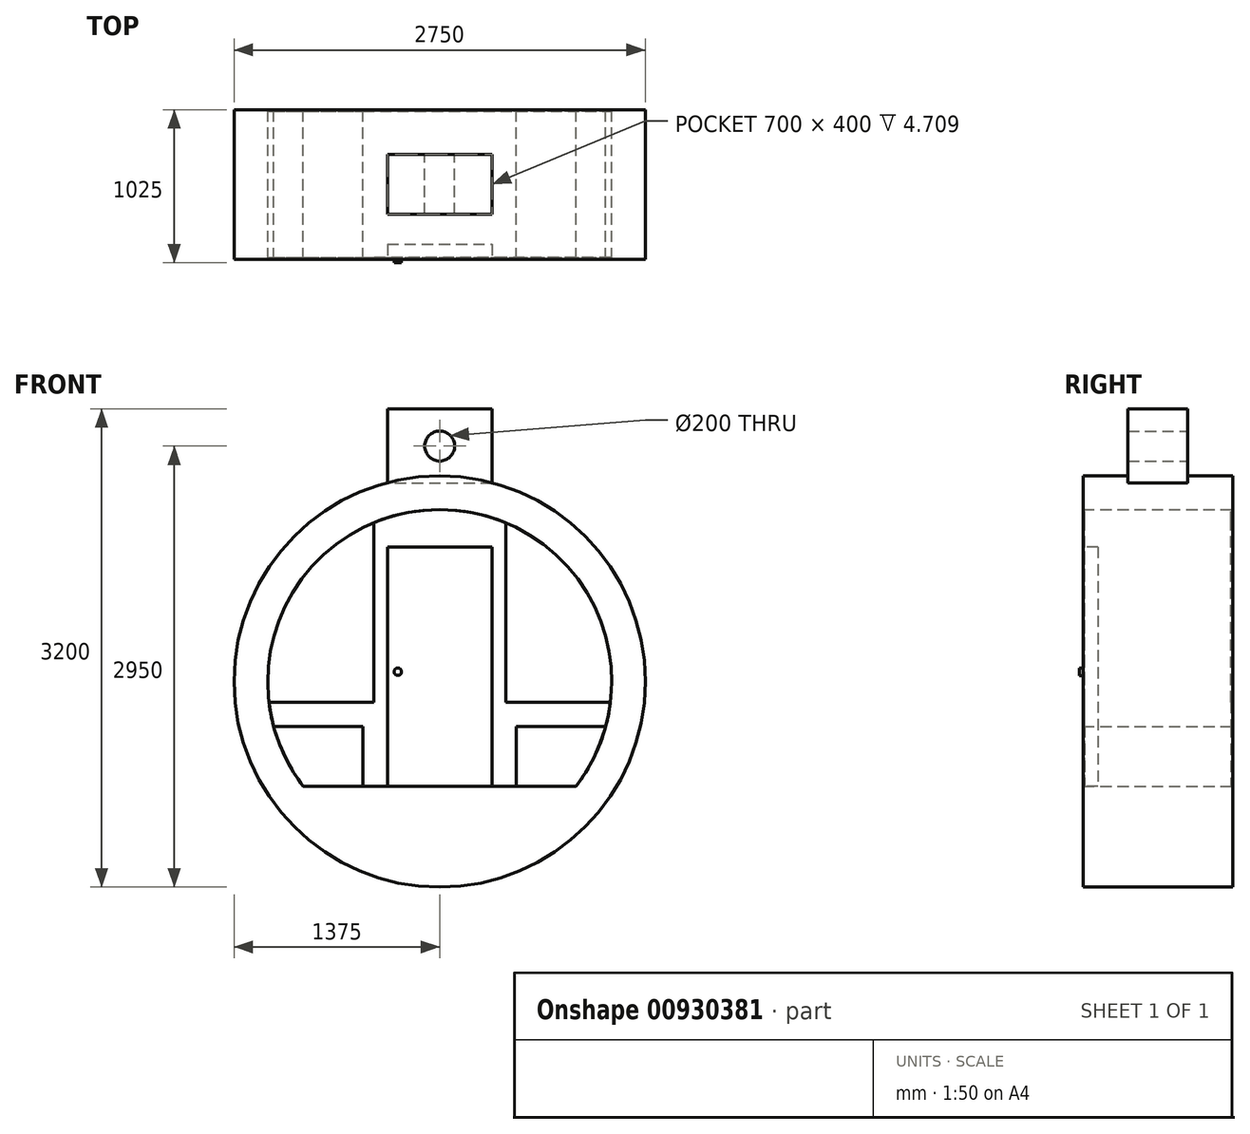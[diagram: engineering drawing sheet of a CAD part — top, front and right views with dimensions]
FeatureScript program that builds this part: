
annotation { "Feature Type Name" : "Feature", "Feature Type Description" : "" }
export const myFeature = defineFeature(function(context is Context, id is Id, definition is map)
    precondition{}
    {
        {
            var Q0;
            Q0=qCreatedBy(makeId("Front.planeOp"),FACE);
            var sketch = newSketch(context, id + "F0", { "sketchPlane" : qUnion([Q0])});
            skLineSegment(sketch, "E0.bottom", {"start": v(350, 3250) * mm, "end": v(-350, 3250) * mm});
            skLineSegment(sketch, "E0.top", {"start": v(350, 2750) * mm, "end": v(-350, 2750) * mm});
            skLineSegment(sketch, "E0.left", {"start": v(350, 3250) * mm, "end": v(350, 2750) * mm});
            skLineSegment(sketch, "E0.right", {"start": v(-350, 3250) * mm, "end": v(-350, 2750) * mm});
            skPoint(sketch, "E0.middle", {"position": v(0, 3000) * mm});
            skCircle(sketch, "E1", {"center": v(0, 3000) * mm, "radius": 100 * mm});
            skSolve(sketch);
        }
        {
            var Q0;
            Q0 = qSketchRegion(id + "F0", true);
            extrude(context, id + "F1", {"entities" : qUnion([Q0]), "endBound" : BoundingType.SYMMETRIC, "depth" : 400 * mm, "offsetDistance" : 25 * mm});
        }
        {
            var Q0;
            Q0=qCreatedBy(makeId("Front.planeOp"),FACE);
            var sketch = newSketch(context, id + "F2", { "sketchPlane" : qUnion([Q0])});
            skLineSegment(sketch, "E2", {"start": v(0, 0) * mm, "end": v(0, 2750) * mm, "construction": true});
            skPoint(sketch, "E3", {"position": v(0, 1375) * mm});
            skCircle(sketch, "E4", {"center": v(0, 1375) * mm, "radius": 1375 * mm});
            skCircle(sketch, "E5", {"center": v(0, 1375) * mm, "radius": 1150 * mm});
            skLineSegment(sketch, "E6", {"start": v(-912.41, 675) * mm, "end": v(912.41, 675) * mm});
            skSolve(sketch);
        }
        {
            var Q0;
            Q0 = qSketchRegion(id + "F2", true);
            var Q1;
            {var subQ0=sQuery(id+"F2.wireOp",EDGE,"E6");Q1=makeQuery(id+"F2.imprint","IMPRINT",FACE,{"disambiguationData":[TD([[makeQuery(id+"F2.imprint","IMPRINT",EDGE,{"derivedFrom":subQ0}),-1.0]])]});}
            extrude(context, id + "F3", {"entities" : qUnion([Q0, Q1]), "operationType" : NewBodyOperationType.ADD, "endBound" : BoundingType.SYMMETRIC, "depth" : 1000 * mm, "offsetDistance" : 25 * mm});
        }
        {
            var Q0;
            Q0=qCreatedBy(makeId("Front.planeOp"),FACE);
            var sketch = newSketch(context, id + "F4", { "sketchPlane" : qUnion([Q0])});
            skLineSegment(sketch, "E7", {"start": v(512.41, 675) * mm, "end": v(512.41, 1075) * mm});
            skLineSegment(sketch, "E8", {"start": v(512.41, 1075) * mm, "end": v(1110.18, 1075) * mm});
            skLineSegment(sketch, "E9.MirrorCS", {"start": v(-512.41, 675) * mm, "end": v(-512.41, 1075) * mm});
            skLineSegment(sketch, "E10.MirrorCS", {"start": v(-512.41, 1075) * mm, "end": v(-1110.18, 1075) * mm});
            skLineSegment(sketch, "E11", {"start": v(512.41, 675) * mm, "end": v(912.41, 675) * mm});
            skArc(sketch, "E12", {"start": v(912.41, 675) * mm, "mid": v(1030.88, 865.32) * mm, "end": v(1110.18, 1075) * mm});
            skArc(sketch, "E13.MirrorCS", {"start": v(-912.41, 675) * mm, "mid": v(-1030.88, 865.32) * mm, "end": v(-1110.18, 1075) * mm});
            skLineSegment(sketch, "E14.MirrorCS", {"start": v(-512.41, 675) * mm, "end": v(-912.41, 675) * mm});
            skSolve(sketch);
        }
        {
            var Q0;
            Q0 = qSketchRegion(id + "F4", true);
            extrude(context, id + "F5", {"entities" : qUnion([Q0]), "endBound" : BoundingType.SYMMETRIC, "depth" : 1000 * mm, "offsetDistance" : 25 * mm});
        }
        {
            var Q0;
            Q0=makeQuery(id+"F3.opExtrude","CAP_FACE",FACE,{"disambiguationData":[OSD([sQuery(id+"F2.wireOp",EDGE,"E4"),sQuery(id+"F2.wireOp",EDGE,"E5"),sQuery(id+"F2.wireOp",EDGE,"E6")])],"isStart":false});
            var sketch = newSketch(context, id + "F6", { "sketchPlane" : qUnion([Q0])});
            skLineSegment(sketch, "E15", {"start": v(-350, 2275) * mm, "end": v(350, 2275) * mm});
            skLineSegment(sketch, "E16", {"start": v(350, 2275) * mm, "end": v(350, 675) * mm});
            skLineSegment(sketch, "E17", {"start": v(350, 675) * mm, "end": v(-350, 675) * mm});
            skLineSegment(sketch, "E18", {"start": v(-350, 675) * mm, "end": v(-350, 2275) * mm});
            skPoint(sketch, "E19", {"position": v(0, 675) * mm});
            skSolve(sketch);
        }
        {
            var Q0;
            Q0 = qSketchRegion(id + "F6", true);
            extrude(context, id + "F7", {"entities" : qUnion([Q0]), "oppositeDirection" : true, "depth" : 100 * mm, "offsetDistance" : 25 * mm});
        }
        {
            var Q0;
            Q0=makeQuery(id+"F7.opExtrude","CAP_FACE",FACE,{"disambiguationData":[OSD([sQuery(id+"F6.wireOp",EDGE,"E15"),sQuery(id+"F6.wireOp",EDGE,"E16"),sQuery(id+"F6.wireOp",EDGE,"E17"),sQuery(id+"F6.wireOp",EDGE,"E18")])],"isStart":true});
            var sketch = newSketch(context, id + "F8", { "sketchPlane" : qUnion([Q0])});
            skCircle(sketch, "E20", {"center": v(-280, 1440.53) * mm, "radius": 25 * mm});
            skSolve(sketch);
        }
        {
            var Q0;
            Q0 = qSketchRegion(id + "F8", true);
            extrude(context, id + "F9", {"entities" : qUnion([Q0]), "depth" : 25 * mm, "offsetDistance" : 25 * mm});
        }
        {
            var Q0;
            Q0=makeQuery(id+"F7.opExtrude","CAP_FACE",FACE,{"disambiguationData":[OSD([sQuery(id+"F6.wireOp",EDGE,"E15"),sQuery(id+"F6.wireOp",EDGE,"E16"),sQuery(id+"F6.wireOp",EDGE,"E17"),sQuery(id+"F6.wireOp",EDGE,"E18")])],"isStart":true});
            var sketch = newSketch(context, id + "F10", { "sketchPlane" : qUnion([Q0])});
            skLineSegment(sketch, "E21", {"start": v(-1141.67, 1236.8) * mm, "end": v(-441.67, 1236.8) * mm});
            skLineSegment(sketch, "E22", {"start": v(-441.67, 1236.8) * mm, "end": v(-441.67, 2436.8) * mm});
            skArc(sketch, "E23", {"start": v(-441.67, 2436.8) * mm, "mid": v(0, 2525) * mm, "end": v(441.67, 2436.8) * mm});
            skArc(sketch, "E24", {"start": v(-1141.67, 1236.8) * mm, "mid": v(-1128.83, 1155.34) * mm, "end": v(-1110.18, 1075) * mm});
            skLineSegment(sketch, "E25.MirrorCS", {"start": v(441.67, 1236.8) * mm, "end": v(441.67, 2436.8) * mm});
            skLineSegment(sketch, "E26.MirrorCS", {"start": v(1141.67, 1236.8) * mm, "end": v(441.67, 1236.8) * mm});
            skArc(sketch, "E27.MirrorCS", {"start": v(1141.67, 1236.8) * mm, "mid": v(1128.83, 1155.34) * mm, "end": v(1110.18, 1075) * mm});
            skLineSegment(sketch, "E28", {"start": v(-1110.18, 1075) * mm, "end": v(-512.41, 1075) * mm});
            skLineSegment(sketch, "E29", {"start": v(-512.41, 1075) * mm, "end": v(-512.41, 675) * mm});
            skLineSegment(sketch, "E30", {"start": v(-512.41, 675) * mm, "end": v(-350, 675) * mm});
            skLineSegment(sketch, "E31", {"start": v(-350, 675) * mm, "end": v(-350, 2275) * mm});
            skLineSegment(sketch, "E32", {"start": v(-350, 2275) * mm, "end": v(350, 2275) * mm});
            skLineSegment(sketch, "E33", {"start": v(350, 2275) * mm, "end": v(350, 675) * mm});
            skLineSegment(sketch, "E34", {"start": v(350, 675) * mm, "end": v(512.41, 675) * mm});
            skLineSegment(sketch, "E35", {"start": v(512.41, 675) * mm, "end": v(512.41, 1075) * mm});
            skLineSegment(sketch, "E36", {"start": v(512.41, 1075) * mm, "end": v(1110.18, 1075) * mm});
            skSolve(sketch);
        }
        {
            var Q0;
            Q0 = qSketchRegion(id + "F10", true);
            extrude(context, id + "F11", {"entities" : qUnion([Q0]), "oppositeDirection" : true, "depth" : 10 * mm, "offsetDistance" : 25 * mm});
        }
        {
            var Q0;
            Q0=makeQuery(id+"F11.opExtrude","SWEPT_BODY",BODY,{"disambiguationData":[OSD([sQuery(id+"F10.wireOp",EDGE,"E21"),sQuery(id+"F10.wireOp",EDGE,"E22"),sQuery(id+"F10.wireOp",EDGE,"E23"),sQuery(id+"F10.wireOp",EDGE,"E24"),sQuery(id+"F10.wireOp",EDGE,"E25.MirrorCS"),sQuery(id+"F10.wireOp",EDGE,"E26.MirrorCS"),sQuery(id+"F10.wireOp",EDGE,"E27.MirrorCS"),sQuery(id+"F10.wireOp",EDGE,"E28"),sQuery(id+"F10.wireOp",EDGE,"E29"),sQuery(id+"F10.wireOp",EDGE,"E30"),sQuery(id+"F10.wireOp",EDGE,"E31"),sQuery(id+"F10.wireOp",EDGE,"E32"),sQuery(id+"F10.wireOp",EDGE,"E33"),sQuery(id+"F10.wireOp",EDGE,"E34"),sQuery(id+"F10.wireOp",EDGE,"E35"),sQuery(id+"F10.wireOp",EDGE,"E36")])]});
            var Q1;
            Q1=qCreatedBy(makeId("Front.planeOp"),FACE);
            mirror(context, id + "F12", {"entities" : qUnion([Q0]), "mirrorPlane" : qUnion([Q1])});
        }
        {
            var Q0;
            Q0=makeQuery(id+"F12.opPattern","COPY",FACE,{"derivedFrom":makeQuery(id+"F11.opExtrude","CAP_FACE",FACE,{"disambiguationData":[OSD([sQuery(id+"F10.wireOp",EDGE,"E21"),sQuery(id+"F10.wireOp",EDGE,"E22"),sQuery(id+"F10.wireOp",EDGE,"E23"),sQuery(id+"F10.wireOp",EDGE,"E24"),sQuery(id+"F10.wireOp",EDGE,"E25.MirrorCS"),sQuery(id+"F10.wireOp",EDGE,"E26.MirrorCS"),sQuery(id+"F10.wireOp",EDGE,"E27.MirrorCS"),sQuery(id+"F10.wireOp",EDGE,"E28"),sQuery(id+"F10.wireOp",EDGE,"E29"),sQuery(id+"F10.wireOp",EDGE,"E30"),sQuery(id+"F10.wireOp",EDGE,"E31"),sQuery(id+"F10.wireOp",EDGE,"E32"),sQuery(id+"F10.wireOp",EDGE,"E33"),sQuery(id+"F10.wireOp",EDGE,"E34"),sQuery(id+"F10.wireOp",EDGE,"E35"),sQuery(id+"F10.wireOp",EDGE,"E36")])],"isStart":true}),"instanceName":"1"});
            var sketch = newSketch(context, id + "F13", { "sketchPlane" : qUnion([Q0])});
            skLineSegment(sketch, "E37.bottom", {"start": v(-350, 2275) * mm, "end": v(350, 2275) * mm});
            skLineSegment(sketch, "E37.top", {"start": v(-350, 675) * mm, "end": v(350, 675) * mm});
            skLineSegment(sketch, "E37.left", {"start": v(-350, 2275) * mm, "end": v(-350, 675) * mm});
            skLineSegment(sketch, "E37.right", {"start": v(350, 2275) * mm, "end": v(350, 675) * mm});
            skSolve(sketch);
        }
        {
            var Q0;
            Q0 = qSketchRegion(id + "F13", true);
            extrude(context, id + "F14", {"entities" : qUnion([Q0]), "operationType" : NewBodyOperationType.ADD, "oppositeDirection" : true, "depth" : 10 * mm, "offsetDistance" : 25 * mm});
        }
        {
            var Q0;
            Q0=makeQuery(id+"F1.opExtrude","SWEPT_BODY",BODY,{"disambiguationData":[OSD([sQuery(id+"F0.wireOp",EDGE,"E0.bottom"),sQuery(id+"F0.wireOp",EDGE,"E0.top"),sQuery(id+"F0.wireOp",EDGE,"E0.left"),sQuery(id+"F0.wireOp",EDGE,"E0.right"),sQuery(id+"F0.wireOp",EDGE,"E1")])]});
            transform(context, id + "F15", {"entities" : qUnion([Q0]), "transformType" : TransformType.TRANSLATION_3D, "dx" : 0 * mm, "dy" : 0 * mm, "dz" : -50 * mm, "makeCopy" : false});
        }
        {
            var Q0;
            Q0=makeQuery(id+"F1.opExtrude","SWEPT_BODY",BODY,{"disambiguationData":[OSD([sQuery(id+"F0.wireOp",EDGE,"E0.bottom"),sQuery(id+"F0.wireOp",EDGE,"E0.top"),sQuery(id+"F0.wireOp",EDGE,"E0.left"),sQuery(id+"F0.wireOp",EDGE,"E0.right"),sQuery(id+"F0.wireOp",EDGE,"E1")])]});
            var Q1;
            Q1=makeQuery(id+"F3.opExtrude","SWEPT_BODY",BODY,{"disambiguationData":[OSD([sQuery(id+"F2.wireOp",EDGE,"E4"),sQuery(id+"F2.wireOp",EDGE,"E5"),sQuery(id+"F2.wireOp",EDGE,"E6")])]});
            booleanBodies(context, id + "F16", {"operationType" : BooleanOperationType.SUBTRACTION, "tools" : qUnion([Q0]), "targets" : qUnion([Q1]), "keepTools" : true});
        }
    });
